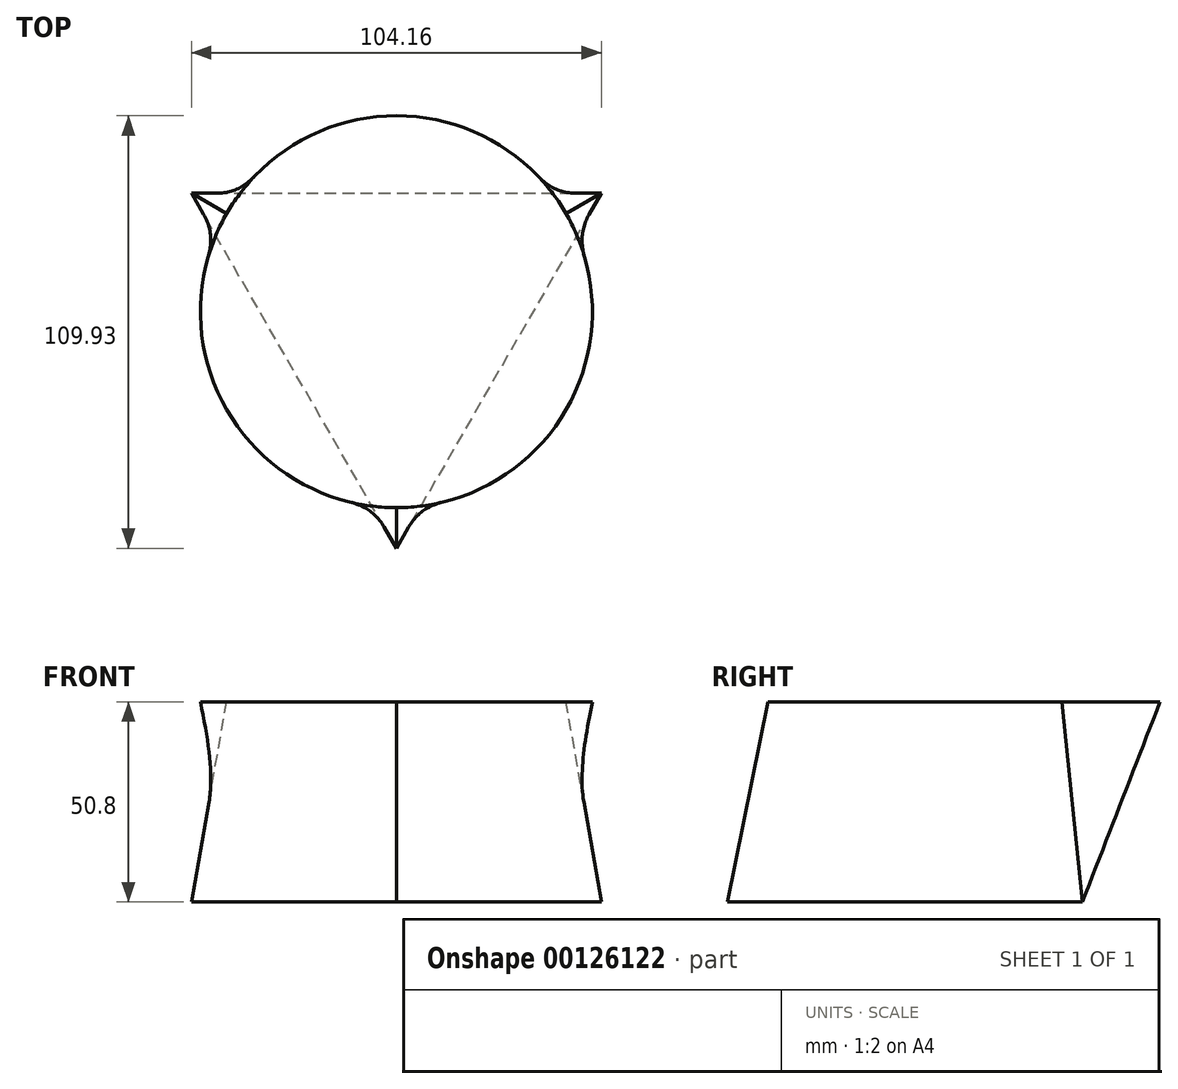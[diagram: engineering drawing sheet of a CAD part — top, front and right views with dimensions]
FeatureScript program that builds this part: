
annotation { "Feature Type Name" : "Feature", "Feature Type Description" : "" }
export const myFeature = defineFeature(function(context is Context, id is Id, definition is map)
    precondition{}
    {
        {
            var Q0;
            Q0=qCreatedBy(makeId("Top.planeOp"),FACE);
            var sketch = newSketch(context, id + "F0", { "sketchPlane" : qUnion([Q0])});
            skCircle(sketch, "E0.cCircle", {"center": v(0, 0) * mm, "radius": 30.07 * mm, "construction": true});
            skLineSegment(sketch, "E0.0", {"start": v(-52.08, 30.07) * mm, "end": v(52.08, 30.07) * mm});
            skLineSegment(sketch, "E0.1", {"start": v(52.08, 30.07) * mm, "end": v(0, -60.14) * mm});
            skLineSegment(sketch, "E0.2", {"start": v(0, -60.14) * mm, "end": v(-52.08, 30.07) * mm});
            skPoint(sketch, "E0.0.midPoint", {"position": v(0, 30.07) * mm});
            skSolve(sketch);
        }
        {
            var Q0;
            Q0=makeQuery(id+"F0.imprint","IMPRINT",FACE,{"disambiguationData":[TD([[makeQuery(id+"F0.imprint","IMPRINT",EDGE,{"derivedFrom":sQuery(id+"F0.wireOp",EDGE,"E0.0")}),-1.0]])]});
            cPlane(context, id + "F1", {"entities" : qUnion([Q0]), "cplaneType" : CPlaneType.OFFSET, "offset" : 50.8 * mm, "width" : 152.4 * mm, "height" : 152.4 * mm});
        }
        {
            var Q0;
            Q0=qCreatedBy(id+"F1.planeOp",FACE);
            var sketch = newSketch(context, id + "F2", { "sketchPlane" : qUnion([Q0])});
            skCircle(sketch, "E1", {"center": v(0, 0) * mm, "radius": 49.8 * mm});
            skSolve(sketch);
        }
        {
            var Q0;
            Q0=makeQuery(id+"F0.imprint","IMPRINT",FACE,{"disambiguationData":[TD([[makeQuery(id+"F0.imprint","IMPRINT",EDGE,{"derivedFrom":sQuery(id+"F0.wireOp",EDGE,"E0.0")}),-1.0]])]});
            var Q1;
            Q1=makeQuery(id+"F2.imprint","IMPRINT",FACE,{"disambiguationData":[TD([[makeQuery(id+"F2.imprint","IMPRINT",EDGE,{"derivedFrom":sQuery(id+"F2.wireOp",EDGE,"E1")}),1.0]])]});
            loft(context, id + "F3", {"sheetProfilesArray" : [{ "sheetProfileEntities" : qUnion([Q0]) }, { "sheetProfileEntities" : qUnion([Q1]) }]});
        }
    });
